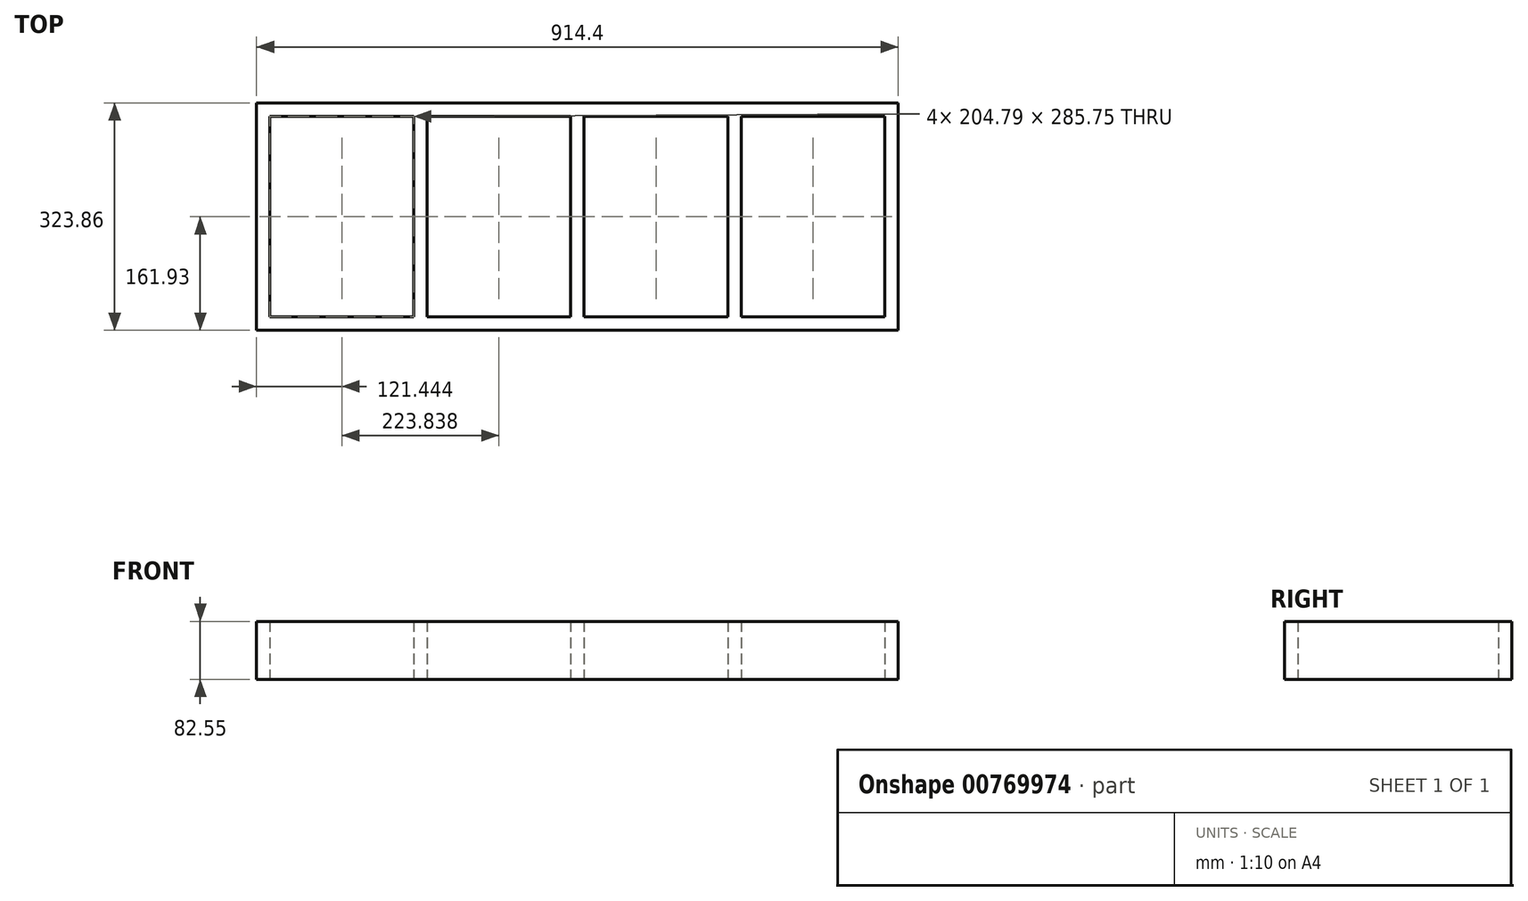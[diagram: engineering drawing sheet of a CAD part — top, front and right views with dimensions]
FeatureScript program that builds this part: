
annotation { "Feature Type Name" : "Feature", "Feature Type Description" : "" }
export const myFeature = defineFeature(function(context is Context, id is Id, definition is map)
    precondition{}
    {
        {
            var Q0;
            Q0=qCreatedBy(makeId("Top.planeOp"),FACE);
            var sketch = newSketch(context, id + "F0", { "sketchPlane" : qUnion([Q0])});
            skLineSegment(sketch, "E0.bottom", {"start": v(457.2, 161.93) * mm, "end": v(-457.2, 161.93) * mm});
            skLineSegment(sketch, "E0.top", {"start": v(457.2, -161.93) * mm, "end": v(-457.2, -161.93) * mm});
            skLineSegment(sketch, "E0.left", {"start": v(457.2, 161.92) * mm, "end": v(457.2, -161.93) * mm});
            skLineSegment(sketch, "E0.right", {"start": v(-457.2, 161.93) * mm, "end": v(-457.2, -161.93) * mm});
            skPoint(sketch, "E0.middle", {"position": v(0, 0) * mm});
            skSolve(sketch);
        }
        {
            var Q0;
            Q0=makeQuery(id+"F0.imprint","IMPRINT",FACE,{"disambiguationData":[TD([[makeQuery(id+"F0.imprint","IMPRINT",EDGE,{"derivedFrom":sQuery(id+"F0.wireOp",EDGE,"E0.bottom")}),1.0]])]});
            extrude(context, id + "F1", {"entities" : qUnion([Q0]), "depth" : 82.55 * mm, "offsetDistance" : 25.4 * mm});
        }
        {
            var Q0;
            Q0=makeQuery(id+"F1.opExtrude","CAP_FACE",FACE,{"disambiguationData":[OSD([sQuery(id+"F0.wireOp",EDGE,"E0.bottom"),sQuery(id+"F0.wireOp",EDGE,"E0.top"),sQuery(id+"F0.wireOp",EDGE,"E0.left"),sQuery(id+"F0.wireOp",EDGE,"E0.right")])],"isStart":true});
            var sketch = newSketch(context, id + "F2", { "sketchPlane" : qUnion([Q0])});
            skLineSegment(sketch, "E1.bottom", {"start": v(438.15, 142.88) * mm, "end": v(-438.15, 142.88) * mm});
            skLineSegment(sketch, "E1.top", {"start": v(438.15, -142.88) * mm, "end": v(-438.15, -142.88) * mm});
            skLineSegment(sketch, "E1.left", {"start": v(438.15, 142.88) * mm, "end": v(438.15, -142.88) * mm});
            skLineSegment(sketch, "E1.right", {"start": v(-438.15, 142.88) * mm, "end": v(-438.15, -142.88) * mm});
            skPoint(sketch, "E1.middle", {"position": v(0, 0) * mm});
            skSolve(sketch);
        }
        {
            var Q0;
            Q0=makeQuery(id+"F2.imprint","IMPRINT",FACE,{"disambiguationData":[TD([[makeQuery(id+"F2.imprint","IMPRINT",EDGE,{"derivedFrom":sQuery(id+"F2.wireOp",EDGE,"E1.bottom")}),1.0]])]});
            extrude(context, id + "F3", {"entities" : qUnion([Q0]), "operationType" : NewBodyOperationType.REMOVE, "oppositeDirection" : true, "depth" : 82.55 * mm, "offsetDistance" : 25.4 * mm});
        }
        {
            var Q0;
            Q0=makeQuery(id+"F1.opExtrude","CAP_FACE",FACE,{"disambiguationData":[OSD([sQuery(id+"F0.wireOp",EDGE,"E0.bottom"),sQuery(id+"F0.wireOp",EDGE,"E0.top"),sQuery(id+"F0.wireOp",EDGE,"E0.left"),sQuery(id+"F0.wireOp",EDGE,"E0.right")])],"isStart":true});
            var sketch = newSketch(context, id + "F4", { "sketchPlane" : qUnion([Q0])});
            skLineSegment(sketch, "E2.bottom", {"start": v(9.53, 142.88) * mm, "end": v(-9.53, 142.88) * mm});
            skLineSegment(sketch, "E2.top", {"start": v(9.53, -142.88) * mm, "end": v(-9.53, -142.88) * mm});
            skLineSegment(sketch, "E2.left", {"start": v(9.53, 142.88) * mm, "end": v(9.53, -142.88) * mm});
            skLineSegment(sketch, "E2.right", {"start": v(-9.53, 142.88) * mm, "end": v(-9.53, -142.88) * mm});
            skPoint(sketch, "E2.middle", {"position": v(0, 0) * mm});
            skSolve(sketch);
        }
        {
            var Q0;
            Q0=makeQuery(id+"F4.imprint","IMPRINT",FACE,{"disambiguationData":[TD([[makeQuery(id+"F4.imprint","IMPRINT",EDGE,{"derivedFrom":sQuery(id+"F4.wireOp",EDGE,"E2.bottom")}),1.0]])]});
            extrude(context, id + "F5", {"entities" : qUnion([Q0]), "operationType" : NewBodyOperationType.ADD, "depth" : -82.55 * mm, "offsetDistance" : 25.4 * mm});
        }
        {
            var Q0;
            Q0=makeQuery(id+"F5.boolean.opBoolean","MERGE",FACE,{"derivedFrom":[makeQuery(id+"F1.opExtrude","CAP_FACE",FACE,{"disambiguationData":[OSD([sQuery(id+"F0.wireOp",EDGE,"E0.bottom"),sQuery(id+"F0.wireOp",EDGE,"E0.top"),sQuery(id+"F0.wireOp",EDGE,"E0.left"),sQuery(id+"F0.wireOp",EDGE,"E0.right")])],"isStart":true}),makeQuery(id+"F5.opExtrude","CAP_FACE",FACE,{"disambiguationData":[OSD([sQuery(id+"F4.wireOp",EDGE,"E2.bottom"),sQuery(id+"F4.wireOp",EDGE,"E2.top"),sQuery(id+"F4.wireOp",EDGE,"E2.left"),sQuery(id+"F4.wireOp",EDGE,"E2.right")])],"isStart":true})]});
            var sketch = newSketch(context, id + "F6", { "sketchPlane" : qUnion([Q0])});
            skLineSegment(sketch, "E3.bottom", {"start": v(-214.31, -142.88) * mm, "end": v(-233.36, -142.88) * mm});
            skLineSegment(sketch, "E3.top", {"start": v(-214.31, 428.63) * mm, "end": v(-233.36, 428.63) * mm});
            skLineSegment(sketch, "E3.left", {"start": v(-214.31, -142.88) * mm, "end": v(-214.31, 428.63) * mm});
            skLineSegment(sketch, "E3.right", {"start": v(-233.36, -142.88) * mm, "end": v(-233.36, 428.63) * mm});
            skPoint(sketch, "E3.middle", {"position": v(-223.84, 142.88) * mm});
            skSolve(sketch);
        }
        {
            var Q0;
            {var subQ0=sQuery(id+"F6.wireOp",EDGE,"E3.bottom");Q0=makeQuery(id+"F6.imprint","IMPRINT",FACE,{"disambiguationData":[TD([[makeQuery(id+"F6.imprint","IMPRINT",EDGE,{"derivedFrom":subQ0}),-1.0]])]});}
            extrude(context, id + "F7", {"entities" : qUnion([Q0]), "operationType" : NewBodyOperationType.ADD, "depth" : -82.55 * mm, "offsetDistance" : 25.4 * mm});
        }
        {
            var Q0;
            Q0=makeQuery(id+"F7.boolean.opBoolean","MERGE",FACE,{"derivedFrom":[makeQuery(id+"F5.boolean.opBoolean","MERGE",FACE,{"derivedFrom":[makeQuery(id+"F1.opExtrude","CAP_FACE",FACE,{"disambiguationData":[OSD([sQuery(id+"F0.wireOp",EDGE,"E0.bottom"),sQuery(id+"F0.wireOp",EDGE,"E0.top"),sQuery(id+"F0.wireOp",EDGE,"E0.left"),sQuery(id+"F0.wireOp",EDGE,"E0.right")])],"isStart":true}),makeQuery(id+"F5.opExtrude","CAP_FACE",FACE,{"disambiguationData":[OSD([sQuery(id+"F4.wireOp",EDGE,"E2.bottom"),sQuery(id+"F4.wireOp",EDGE,"E2.top"),sQuery(id+"F4.wireOp",EDGE,"E2.left"),sQuery(id+"F4.wireOp",EDGE,"E2.right")])],"isStart":true})]}),makeQuery(id+"F7.opExtrude","CAP_FACE",FACE,{"disambiguationData":[OSD([sQuery(id+"F2.wireOp",EDGE,"E1.bottom"),sQuery(id+"F6.wireOp",EDGE,"E3.bottom"),sQuery(id+"F6.wireOp",EDGE,"E3.left"),sQuery(id+"F6.wireOp",EDGE,"E3.right")])],"isStart":true})]});
            var sketch = newSketch(context, id + "F8", { "sketchPlane" : qUnion([Q0])});
            skLineSegment(sketch, "E4.bottom", {"start": v(233.36, -142.88) * mm, "end": v(214.31, -142.88) * mm});
            skLineSegment(sketch, "E4.top", {"start": v(233.36, 428.63) * mm, "end": v(214.31, 428.63) * mm});
            skLineSegment(sketch, "E4.left", {"start": v(233.36, -142.88) * mm, "end": v(233.36, 428.63) * mm});
            skLineSegment(sketch, "E4.right", {"start": v(214.31, -142.88) * mm, "end": v(214.31, 428.63) * mm});
            skPoint(sketch, "E4.middle", {"position": v(223.84, 142.88) * mm});
            skSolve(sketch);
        }
        {
            var Q0;
            {var subQ0=sQuery(id+"F8.wireOp",EDGE,"E4.bottom");Q0=makeQuery(id+"F8.imprint","IMPRINT",FACE,{"disambiguationData":[TD([[makeQuery(id+"F8.imprint","IMPRINT",EDGE,{"derivedFrom":subQ0}),-1.0]])]});}
            extrude(context, id + "F9", {"entities" : qUnion([Q0]), "operationType" : NewBodyOperationType.ADD, "depth" : -82.55 * mm, "offsetDistance" : 25.4 * mm});
        }
    });
